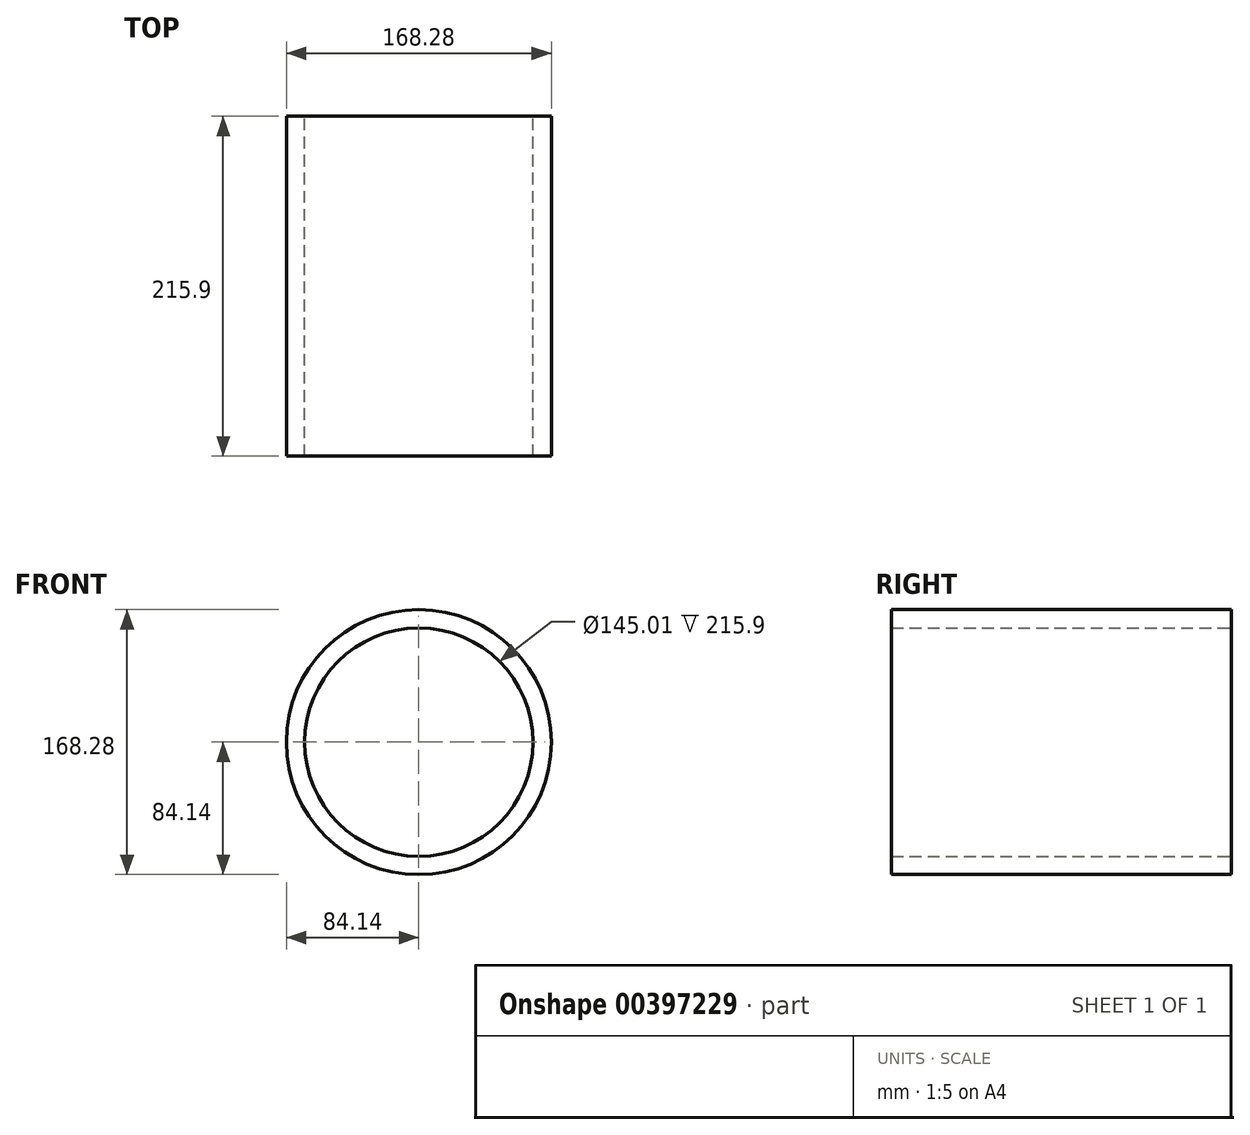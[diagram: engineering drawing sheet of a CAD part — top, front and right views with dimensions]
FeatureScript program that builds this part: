
annotation { "Feature Type Name" : "Feature", "Feature Type Description" : "" }
export const myFeature = defineFeature(function(context is Context, id is Id, definition is map)
    precondition{}
    {
        {
            var Q0;
            Q0=qCreatedBy(makeId("Front.planeOp"),FACE);
            var sketch = newSketch(context, id + "F0", { "sketchPlane" : qUnion([Q0])});
            skCircle(sketch, "E0", {"center": v(0, 0) * mm, "radius": 84.14 * mm});
            skCircle(sketch, "E1", {"center": v(0, 0) * mm, "radius": 72.5 * mm});
            skSolve(sketch);
        }
        {
            var Q0;
            Q0=qSketchRegion(id+"F0",true);
            extrude(context, id + "F1", {"entities" : qUnion([Q0]), "depth" : 215.9 * mm});
        }
    });
